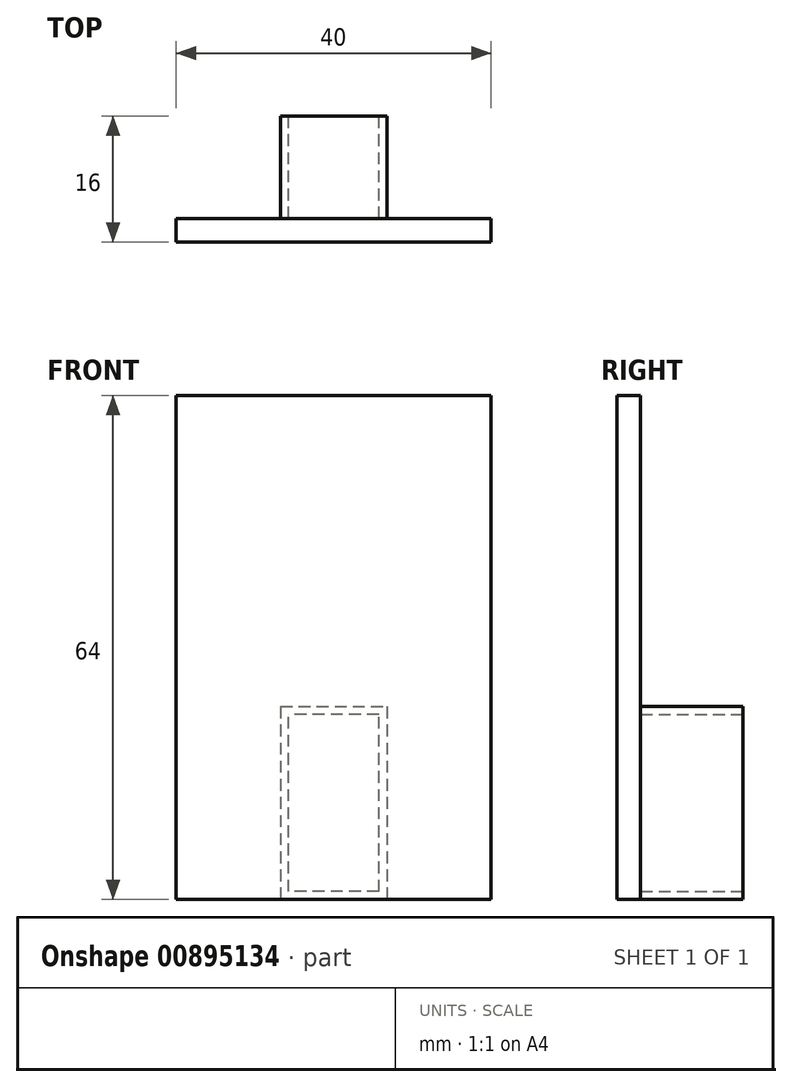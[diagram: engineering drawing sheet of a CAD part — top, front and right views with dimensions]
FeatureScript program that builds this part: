
annotation { "Feature Type Name" : "Feature", "Feature Type Description" : "" }
export const myFeature = defineFeature(function(context is Context, id is Id, definition is map)
    precondition{}
    {
        {
            var Q0;
            Q0=qCreatedBy(makeId("Front.planeOp"),FACE);
            var sketch = newSketch(context, id + "F0", { "sketchPlane" : qUnion([Q0])});
            skLineSegment(sketch, "E0.bottom", {"start": v(-6.75, 12.25) * mm, "end": v(6.75, 12.25) * mm});
            skLineSegment(sketch, "E0.top", {"start": v(-6.75, -12.25) * mm, "end": v(6.75, -12.25) * mm});
            skLineSegment(sketch, "E0.left", {"start": v(-6.75, 12.25) * mm, "end": v(-6.75, -12.25) * mm});
            skLineSegment(sketch, "E0.right", {"start": v(6.75, 12.25) * mm, "end": v(6.75, -12.25) * mm});
            skPoint(sketch, "E0.middle", {"position": v(0, 0) * mm});
            skLineSegment(sketch, "E1.bottom", {"start": v(5.75, -11.25) * mm, "end": v(-5.75, -11.25) * mm});
            skLineSegment(sketch, "E1.top", {"start": v(5.75, 11.25) * mm, "end": v(-5.75, 11.25) * mm});
            skLineSegment(sketch, "E1.left", {"start": v(5.75, -11.25) * mm, "end": v(5.75, 11.25) * mm});
            skLineSegment(sketch, "E1.right", {"start": v(-5.75, -11.25) * mm, "end": v(-5.75, 11.25) * mm});
            skSolve(sketch);
        }
        {
            var Q0;
            Q0=makeQuery(id+"F0.imprint","IMPRINT",FACE,{"disambiguationData":[TD([[makeQuery(id+"F0.imprint","IMPRINT",EDGE,{"derivedFrom":sQuery(id+"F0.wireOp",EDGE,"E0.bottom")}),-1.0]])]});
            extrude(context, id + "F1", {"entities" : qUnion([Q0]), "depth" : 13 * mm, "offsetDistance" : 25 * mm});
        }
        {
            var Q0;
            Q0=makeQuery(id+"F1.opExtrude","CAP_FACE",FACE,{"disambiguationData":[OSD([sQuery(id+"F0.wireOp",EDGE,"E0.bottom"),sQuery(id+"F0.wireOp",EDGE,"E0.top"),sQuery(id+"F0.wireOp",EDGE,"E0.left"),sQuery(id+"F0.wireOp",EDGE,"E0.right"),sQuery(id+"F0.wireOp",EDGE,"E1.bottom"),sQuery(id+"F0.wireOp",EDGE,"E1.top"),sQuery(id+"F0.wireOp",EDGE,"E1.left"),sQuery(id+"F0.wireOp",EDGE,"E1.right")])],"isStart":false});
            var sketch = newSketch(context, id + "F2", { "sketchPlane" : qUnion([Q0])});
            skLineSegment(sketch, "E2.bottom", {"start": v(-20, -12.25) * mm, "end": v(20, -12.25) * mm});
            skLineSegment(sketch, "E2.top", {"start": v(-20, 51.75) * mm, "end": v(20, 51.75) * mm});
            skLineSegment(sketch, "E2.left", {"start": v(-20, -12.25) * mm, "end": v(-20, 51.75) * mm});
            skLineSegment(sketch, "E2.right", {"start": v(20, -12.25) * mm, "end": v(20, 51.75) * mm});
            skSolve(sketch);
        }
        {
            var Q0;
            Q0=makeQuery(id+"F2.imprint","IMPRINT",FACE,{"disambiguationData":[TD([[makeQuery(id+"F2.imprint","IMPRINT",EDGE,{"derivedFrom":makeQuery(id+"F1.opExtrude","CAP_EDGE",EDGE,{"disambiguationData":[OSD([sQuery(id+"F0.wireOp",EDGE,"E1.bottom")])],"isStart":false})}),-1.0]])]});
            var Q1;
            Q1=makeQuery(id+"F2.imprint","IMPRINT",FACE,{"disambiguationData":[TD([[makeQuery(id+"F2.imprint","IMPRINT",EDGE,{"derivedFrom":sQuery(id+"F2.wireOp",EDGE,"E2.top")}),-1.0]])]});
            var Q2;
            Q2=makeQuery(id+"F2.imprint","IMPRINT",FACE,{"disambiguationData":[TD([[makeQuery(id+"F2.imprint","IMPRINT",EDGE,{"derivedFrom":makeQuery(id+"F1.opExtrude","CAP_EDGE",EDGE,{"disambiguationData":[OSD([sQuery(id+"F0.wireOp",EDGE,"E0.bottom")])],"isStart":false})}),-1.0]])]});
            extrude(context, id + "F3", {"entities" : qUnion([Q0, Q1, Q2]), "operationType" : NewBodyOperationType.ADD, "depth" : 3 * mm, "offsetDistance" : 25 * mm});
        }
    });
